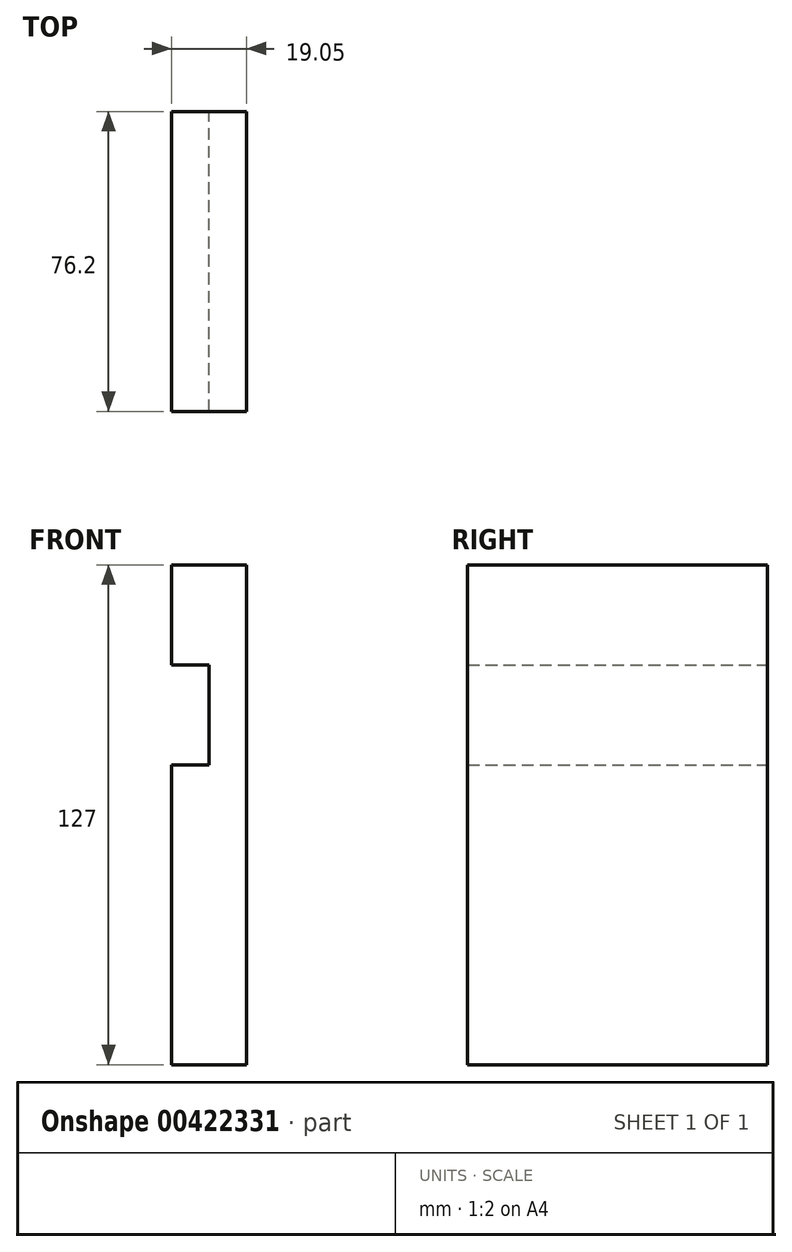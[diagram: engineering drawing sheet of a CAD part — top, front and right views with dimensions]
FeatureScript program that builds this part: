
annotation { "Feature Type Name" : "Feature", "Feature Type Description" : "" }
export const myFeature = defineFeature(function(context is Context, id is Id, definition is map)
    precondition{}
    {
        {
            var Q0;
            Q0=qCreatedBy(makeId("Front.planeOp"),FACE);
            var sketch = newSketch(context, id + "F0", { "sketchPlane" : qUnion([Q0])});
            skLineSegment(sketch, "E0", {"start": v(28.23, -64.34) * mm, "end": v(28.23, 62.66) * mm});
            skLineSegment(sketch, "E1", {"start": v(28.23, 62.66) * mm, "end": v(9.18, 62.66) * mm});
            skLineSegment(sketch, "E2", {"start": v(9.18, 62.66) * mm, "end": v(9.18, 37.26) * mm});
            skLineSegment(sketch, "E3", {"start": v(9.18, 37.26) * mm, "end": v(18.7, 37.26) * mm});
            skLineSegment(sketch, "E4", {"start": v(18.7, 37.26) * mm, "end": v(18.7, 11.86) * mm});
            skLineSegment(sketch, "E5", {"start": v(18.7, 11.86) * mm, "end": v(9.18, 11.86) * mm});
            skLineSegment(sketch, "E6", {"start": v(28.23, -64.34) * mm, "end": v(9.18, -64.34) * mm});
            skLineSegment(sketch, "E7", {"start": v(9.18, 11.86) * mm, "end": v(9.18, -64.34) * mm});
            skSolve(sketch);
        }
        {
            var Q0;
            Q0 = qSketchRegion(id + "F0", true);
            extrude(context, id + "F1", {"entities" : qUnion([Q0]), "depth" : 76.2 * mm});
        }
    });
